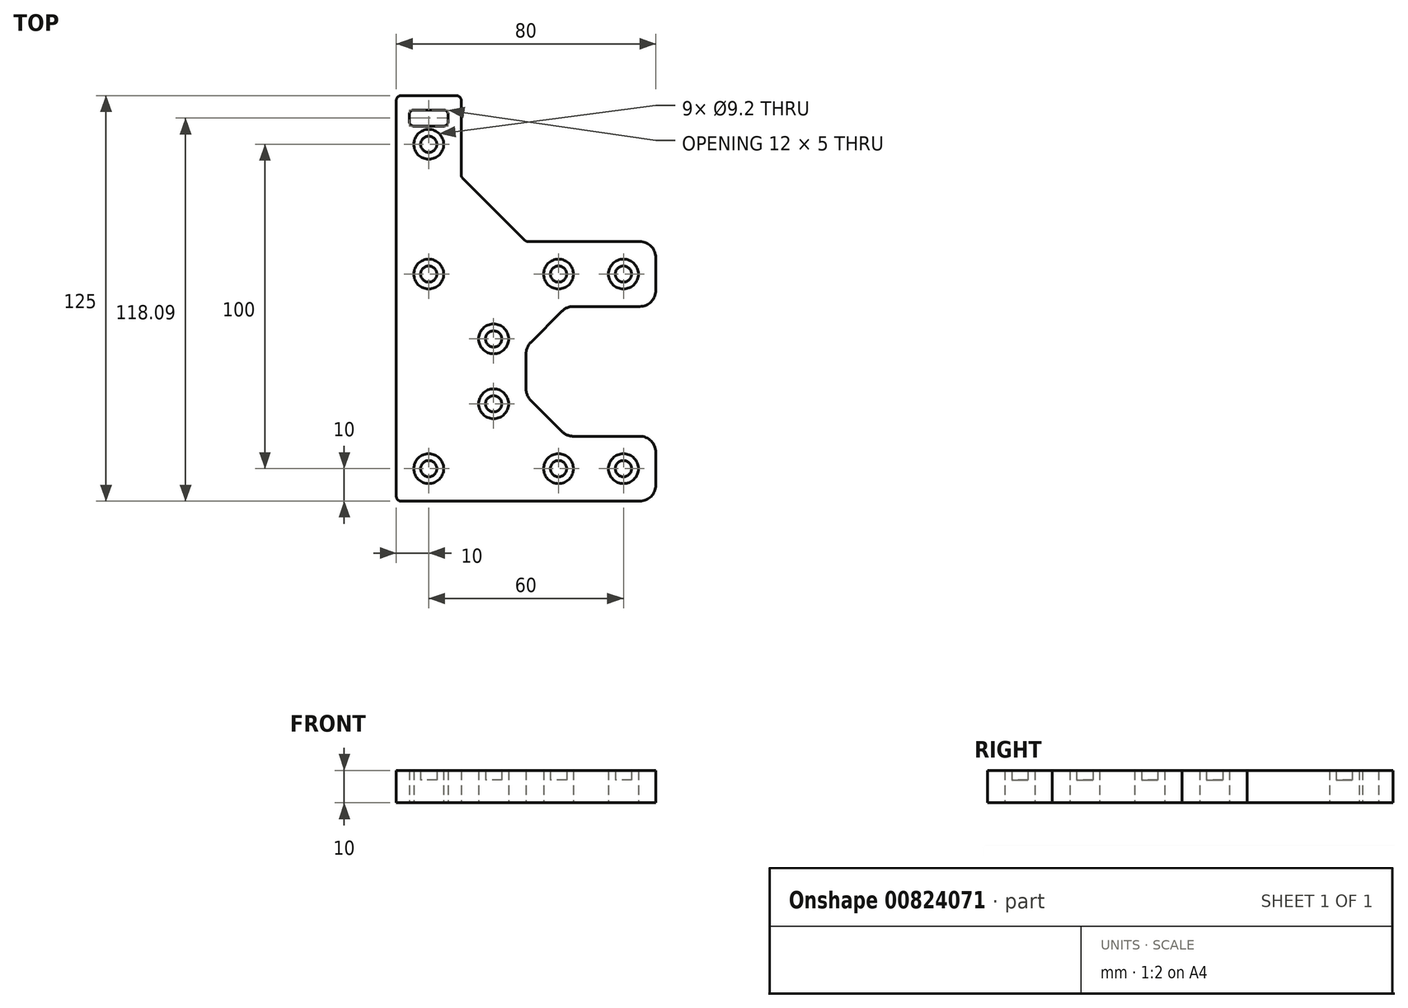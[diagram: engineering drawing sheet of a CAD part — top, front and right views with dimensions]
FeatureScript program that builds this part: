
annotation { "Feature Type Name" : "Feature", "Feature Type Description" : "" }
export const myFeature = defineFeature(function(context is Context, id is Id, definition is map)
    precondition{}
    {
        {
            var Q0;
            Q0=qCreatedBy(makeId("Top.planeOp"),FACE);
            var sketch = newSketch(context, id + "F0", { "sketchPlane" : qUnion([Q0])});
            skLineSegment(sketch, "E0", {"start": v(-38.5, -62.5) * mm, "end": v(35, -62.5) * mm});
            skLineSegment(sketch, "E1", {"start": v(-40, 61) * mm, "end": v(-40, -61) * mm});
            skLineSegment(sketch, "E2", {"start": v(35, -42.5) * mm, "end": v(14.57, -42.5) * mm});
            skLineSegment(sketch, "E3", {"start": v(-36, 56.65) * mm, "end": v(-36, 54.53) * mm});
            skLineSegment(sketch, "E4", {"start": v(-24, 54.53) * mm, "end": v(-24, 56.65) * mm});
            skLineSegment(sketch, "E5", {"start": v(-20, 61) * mm, "end": v(-20, 38.12) * mm});
            skLineSegment(sketch, "E6", {"start": v(1.46, -31.46) * mm, "end": v(11.04, -41.04) * mm});
            skLineSegment(sketch, "E7", {"start": v(0, -17.07) * mm, "end": v(0, -27.93) * mm});
            skLineSegment(sketch, "E8", {"start": v(35, -2.5) * mm, "end": v(14.57, -2.5) * mm});
            skLineSegment(sketch, "E9", {"start": v(11.04, -3.96) * mm, "end": v(1.46, -13.54) * mm});
            skLineSegment(sketch, "E10", {"start": v(-19.56, 37.06) * mm, "end": v(-0.44, 17.94) * mm});
            skLineSegment(sketch, "E11", {"start": v(35, 17.5) * mm, "end": v(0.62, 17.5) * mm});
            skLineSegment(sketch, "E12", {"start": v(40, -57.5) * mm, "end": v(40, -47.5) * mm});
            skLineSegment(sketch, "E13", {"start": v(40, 2.5) * mm, "end": v(40, 12.5) * mm});
            skLineSegment(sketch, "E14", {"start": v(-34.56, 53.1) * mm, "end": v(-25.44, 53.1) * mm});
            skLineSegment(sketch, "E15", {"start": v(-25.44, 58.1) * mm, "end": v(-34.56, 58.1) * mm});
            skLineSegment(sketch, "E16", {"start": v(-21.5, 62.5) * mm, "end": v(-38.5, 62.5) * mm});
            skArc(sketch, "E17", {"start": v(11.04, -41.04) * mm, "mid": v(12.66, -42.12) * mm, "end": v(14.57, -42.5) * mm});
            skArc(sketch, "E18", {"start": v(0, -27.93) * mm, "mid": v(0.38, -29.84) * mm, "end": v(1.46, -31.46) * mm});
            skArc(sketch, "E19", {"start": v(1.46, -13.54) * mm, "mid": v(0.38, -15.16) * mm, "end": v(0, -17.07) * mm});
            skArc(sketch, "E20", {"start": v(14.57, -2.5) * mm, "mid": v(12.66, -2.88) * mm, "end": v(11.04, -3.96) * mm});
            skArc(sketch, "E21", {"start": v(35, -62.5) * mm, "mid": v(38.54, -61.04) * mm, "end": v(40, -57.5) * mm});
            skArc(sketch, "E22", {"start": v(40, -47.5) * mm, "mid": v(38.54, -43.96) * mm, "end": v(35, -42.5) * mm});
            skArc(sketch, "E23", {"start": v(40, 12.5) * mm, "mid": v(38.54, 16.04) * mm, "end": v(35, 17.5) * mm});
            skArc(sketch, "E24", {"start": v(35, -2.5) * mm, "mid": v(38.54, -1.04) * mm, "end": v(40, 2.5) * mm});
            skCircle(sketch, "E25", {"center": v(-30, 7.5) * mm, "radius": 2.5 * mm});
            skCircle(sketch, "E26", {"center": v(-10, -32.5) * mm, "radius": 2.5 * mm});
            skCircle(sketch, "E27", {"center": v(-10, -12.5) * mm, "radius": 2.5 * mm});
            skCircle(sketch, "E28", {"center": v(10, 7.5) * mm, "radius": 2.5 * mm});
            skCircle(sketch, "E29", {"center": v(30, 7.5) * mm, "radius": 2.5 * mm});
            skCircle(sketch, "E30", {"center": v(30, -52.5) * mm, "radius": 2.5 * mm});
            skCircle(sketch, "E31", {"center": v(10, -52.5) * mm, "radius": 2.5 * mm});
            skCircle(sketch, "E32", {"center": v(-30, -52.5) * mm, "radius": 2.5 * mm});
            skCircle(sketch, "E33", {"center": v(-30, 47.5) * mm, "radius": 2.5 * mm});
            skArc(sketch, "E34", {"start": v(-20, 38.12) * mm, "mid": v(-19.89, 37.55) * mm, "end": v(-19.56, 37.06) * mm});
            skArc(sketch, "E35", {"start": v(-0.44, 17.94) * mm, "mid": v(0.05, 17.61) * mm, "end": v(0.62, 17.5) * mm});
            skArc(sketch, "E36", {"start": v(-20, 61) * mm, "mid": v(-20.44, 62.06) * mm, "end": v(-21.5, 62.5) * mm});
            skArc(sketch, "E37", {"start": v(-38.5, 62.5) * mm, "mid": v(-39.56, 62.06) * mm, "end": v(-40, 61) * mm});
            skArc(sketch, "E38", {"start": v(-40, -61) * mm, "mid": v(-39.56, -62.06) * mm, "end": v(-38.5, -62.5) * mm});
            skArc(sketch, "E39", {"start": v(-34.56, 58.1) * mm, "mid": v(-35.58, 57.67) * mm, "end": v(-36, 56.65) * mm});
            skArc(sketch, "E40", {"start": v(-24, 56.65) * mm, "mid": v(-24.42, 57.67) * mm, "end": v(-25.44, 58.1) * mm});
            skArc(sketch, "E41", {"start": v(-25.44, 53.1) * mm, "mid": v(-24.42, 53.51) * mm, "end": v(-24, 54.53) * mm});
            skArc(sketch, "E42", {"start": v(-36, 54.53) * mm, "mid": v(-35.58, 53.51) * mm, "end": v(-34.56, 53.1) * mm});
            skCircle(sketch, "E43.0", {"center": v(-30, -52.5) * mm, "radius": 4.6 * mm});
            skCircle(sketch, "E44.0", {"center": v(10, -52.5) * mm, "radius": 4.6 * mm});
            skCircle(sketch, "E45.0", {"center": v(30, -52.5) * mm, "radius": 4.6 * mm});
            skCircle(sketch, "E46.0", {"center": v(-10, -32.5) * mm, "radius": 4.6 * mm});
            skCircle(sketch, "E47.0", {"center": v(-10, -12.5) * mm, "radius": 4.6 * mm});
            skCircle(sketch, "E48.0", {"center": v(-30, 7.5) * mm, "radius": 4.6 * mm});
            skCircle(sketch, "E49.0", {"center": v(10, 7.5) * mm, "radius": 4.6 * mm});
            skCircle(sketch, "E50.0", {"center": v(30, 7.5) * mm, "radius": 4.6 * mm});
            skCircle(sketch, "E51.0", {"center": v(-30, 47.5) * mm, "radius": 4.6 * mm});
            skSolve(sketch);
        }
        {
            var Q0;
            Q0 = qSketchRegion(id + "F0", true);
            var Q1;
            Q1=makeQuery(id+"F0.imprint","IMPRINT",FACE,{"disambiguationData":[TD([[makeQuery(id+"F0.imprint","IMPRINT",EDGE,{"derivedFrom":sQuery(id+"F0.wireOp",EDGE,"E33")}),1.0]])]});
            var Q2;
            Q2=makeQuery(id+"F0.imprint","IMPRINT",FACE,{"disambiguationData":[TD([[makeQuery(id+"F0.imprint","IMPRINT",EDGE,{"derivedFrom":sQuery(id+"F0.wireOp",EDGE,"E25")}),1.0]])]});
            var Q3;
            Q3=makeQuery(id+"F0.imprint","IMPRINT",FACE,{"disambiguationData":[TD([[makeQuery(id+"F0.imprint","IMPRINT",EDGE,{"derivedFrom":sQuery(id+"F0.wireOp",EDGE,"E32")}),1.0]])]});
            var Q4;
            Q4=makeQuery(id+"F0.imprint","IMPRINT",FACE,{"disambiguationData":[TD([[makeQuery(id+"F0.imprint","IMPRINT",EDGE,{"derivedFrom":sQuery(id+"F0.wireOp",EDGE,"E26")}),1.0]])]});
            var Q5;
            Q5=makeQuery(id+"F0.imprint","IMPRINT",FACE,{"disambiguationData":[TD([[makeQuery(id+"F0.imprint","IMPRINT",EDGE,{"derivedFrom":sQuery(id+"F0.wireOp",EDGE,"E27")}),1.0]])]});
            var Q6;
            Q6=makeQuery(id+"F0.imprint","IMPRINT",FACE,{"disambiguationData":[TD([[makeQuery(id+"F0.imprint","IMPRINT",EDGE,{"derivedFrom":sQuery(id+"F0.wireOp",EDGE,"E28")}),1.0]])]});
            var Q7;
            Q7=makeQuery(id+"F0.imprint","IMPRINT",FACE,{"disambiguationData":[TD([[makeQuery(id+"F0.imprint","IMPRINT",EDGE,{"derivedFrom":sQuery(id+"F0.wireOp",EDGE,"E29")}),1.0]])]});
            var Q8;
            Q8=makeQuery(id+"F0.imprint","IMPRINT",FACE,{"disambiguationData":[TD([[makeQuery(id+"F0.imprint","IMPRINT",EDGE,{"derivedFrom":sQuery(id+"F0.wireOp",EDGE,"E31")}),1.0]])]});
            var Q9;
            Q9=makeQuery(id+"F0.imprint","IMPRINT",FACE,{"disambiguationData":[TD([[makeQuery(id+"F0.imprint","IMPRINT",EDGE,{"derivedFrom":sQuery(id+"F0.wireOp",EDGE,"E30")}),1.0]])]});
            extrude(context, id + "F1", {"entities" : qUnion([Q0, Q1, Q2, Q3, Q4, Q5, Q6, Q7, Q8, Q9]), "depth" : 10 * mm, "offsetDistance" : 25 * mm});
        }
        {
            var Q0;
            Q0=makeQuery(id+"F0.imprint","IMPRINT",FACE,{"disambiguationData":[TD([[makeQuery(id+"F0.imprint","IMPRINT",EDGE,{"derivedFrom":sQuery(id+"F0.wireOp",EDGE,"E29")}),1.0]])]});
            var Q1;
            Q1=makeQuery(id+"F0.imprint","IMPRINT",FACE,{"disambiguationData":[TD([[makeQuery(id+"F0.imprint","IMPRINT",EDGE,{"derivedFrom":sQuery(id+"F0.wireOp",EDGE,"E28")}),1.0]])]});
            var Q2;
            Q2=makeQuery(id+"F0.imprint","IMPRINT",FACE,{"disambiguationData":[TD([[makeQuery(id+"F0.imprint","IMPRINT",EDGE,{"derivedFrom":sQuery(id+"F0.wireOp",EDGE,"E30")}),1.0]])]});
            var Q3;
            Q3=makeQuery(id+"F0.imprint","IMPRINT",FACE,{"disambiguationData":[TD([[makeQuery(id+"F0.imprint","IMPRINT",EDGE,{"derivedFrom":sQuery(id+"F0.wireOp",EDGE,"E31")}),1.0]])]});
            var Q4;
            Q4=makeQuery(id+"F0.imprint","IMPRINT",FACE,{"disambiguationData":[TD([[makeQuery(id+"F0.imprint","IMPRINT",EDGE,{"derivedFrom":sQuery(id+"F0.wireOp",EDGE,"E26")}),1.0]])]});
            var Q5;
            Q5=makeQuery(id+"F0.imprint","IMPRINT",FACE,{"disambiguationData":[TD([[makeQuery(id+"F0.imprint","IMPRINT",EDGE,{"derivedFrom":sQuery(id+"F0.wireOp",EDGE,"E27")}),1.0]])]});
            var Q6;
            Q6=makeQuery(id+"F0.imprint","IMPRINT",FACE,{"disambiguationData":[TD([[makeQuery(id+"F0.imprint","IMPRINT",EDGE,{"derivedFrom":sQuery(id+"F0.wireOp",EDGE,"E25")}),1.0]])]});
            var Q7;
            Q7=makeQuery(id+"F0.imprint","IMPRINT",FACE,{"disambiguationData":[TD([[makeQuery(id+"F0.imprint","IMPRINT",EDGE,{"derivedFrom":sQuery(id+"F0.wireOp",EDGE,"E32")}),1.0]])]});
            var Q8;
            Q8=makeQuery(id+"F0.imprint","IMPRINT",FACE,{"disambiguationData":[TD([[makeQuery(id+"F0.imprint","IMPRINT",EDGE,{"derivedFrom":sQuery(id+"F0.wireOp",EDGE,"E33")}),1.0]])]});
            var Q9;
            Q9=makeQuery(id+"F1.opExtrude","CAP_FACE",FACE,{"disambiguationData":[OSD([sQuery(id+"F0.wireOp",EDGE,"E0"),sQuery(id+"F0.wireOp",EDGE,"E1"),sQuery(id+"F0.wireOp",EDGE,"E2"),sQuery(id+"F0.wireOp",EDGE,"E3"),sQuery(id+"F0.wireOp",EDGE,"E4"),sQuery(id+"F0.wireOp",EDGE,"E5"),sQuery(id+"F0.wireOp",EDGE,"E6"),sQuery(id+"F0.wireOp",EDGE,"E7"),sQuery(id+"F0.wireOp",EDGE,"E8"),sQuery(id+"F0.wireOp",EDGE,"E9"),sQuery(id+"F0.wireOp",EDGE,"E10"),sQuery(id+"F0.wireOp",EDGE,"E11"),sQuery(id+"F0.wireOp",EDGE,"E12"),sQuery(id+"F0.wireOp",EDGE,"E13"),sQuery(id+"F0.wireOp",EDGE,"E14"),sQuery(id+"F0.wireOp",EDGE,"E15"),sQuery(id+"F0.wireOp",EDGE,"E16"),sQuery(id+"F0.wireOp",EDGE,"E17"),sQuery(id+"F0.wireOp",EDGE,"E18"),sQuery(id+"F0.wireOp",EDGE,"E19"),sQuery(id+"F0.wireOp",EDGE,"E20"),sQuery(id+"F0.wireOp",EDGE,"E21"),sQuery(id+"F0.wireOp",EDGE,"E22"),sQuery(id+"F0.wireOp",EDGE,"E23"),sQuery(id+"F0.wireOp",EDGE,"E24"),sQuery(id+"F0.wireOp",EDGE,"E25"),sQuery(id+"F0.wireOp",EDGE,"E26"),sQuery(id+"F0.wireOp",EDGE,"E27"),sQuery(id+"F0.wireOp",EDGE,"E28"),sQuery(id+"F0.wireOp",EDGE,"E29"),sQuery(id+"F0.wireOp",EDGE,"E30"),sQuery(id+"F0.wireOp",EDGE,"E31"),sQuery(id+"F0.wireOp",EDGE,"E32"),sQuery(id+"F0.wireOp",EDGE,"E33"),sQuery(id+"F0.wireOp",EDGE,"E34"),sQuery(id+"F0.wireOp",EDGE,"E35"),sQuery(id+"F0.wireOp",EDGE,"E36"),sQuery(id+"F0.wireOp",EDGE,"E37"),sQuery(id+"F0.wireOp",EDGE,"E38"),sQuery(id+"F0.wireOp",EDGE,"E39"),sQuery(id+"F0.wireOp",EDGE,"E40"),sQuery(id+"F0.wireOp",EDGE,"E41"),sQuery(id+"F0.wireOp",EDGE,"E42")])],"isStart":false});
            extrude(context, id + "F2", {"entities" : qUnion([Q0, Q1, Q2, Q3, Q4, Q5, Q6, Q7, Q8]), "operationType" : NewBodyOperationType.REMOVE, "endBound" : BoundingType.UP_TO_SURFACE, "depth" : 6 * mm, "endBoundEntityFace" : qUnion([Q9]), "hasOffset" : true, "offsetDistance" : 3 * mm});
        }
    });
